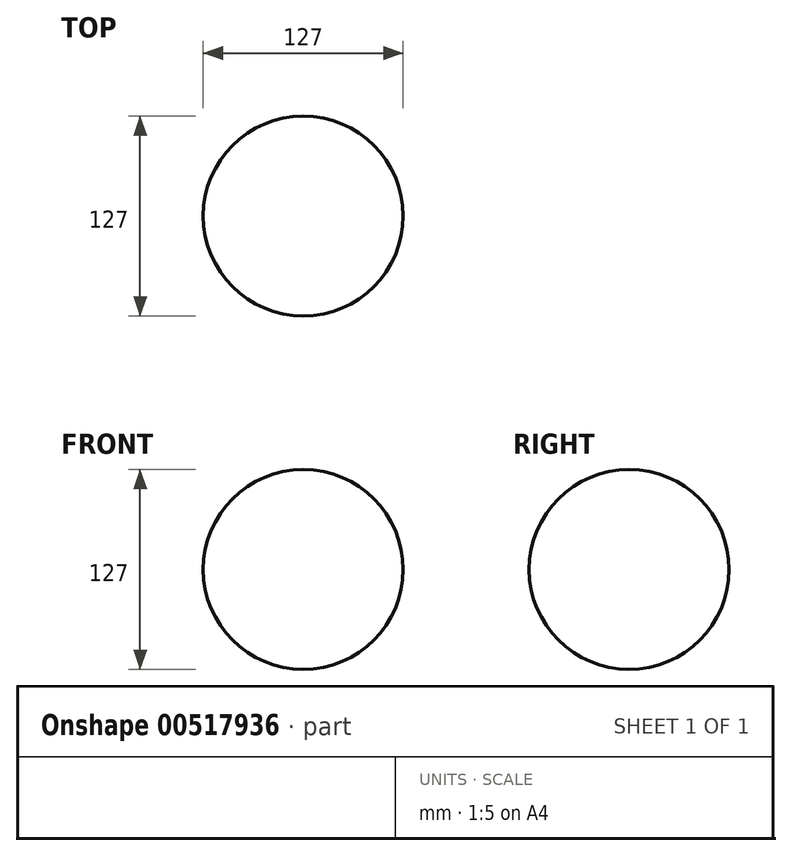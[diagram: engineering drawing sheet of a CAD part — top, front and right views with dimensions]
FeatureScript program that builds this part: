
annotation { "Feature Type Name" : "Feature", "Feature Type Description" : "" }
export const myFeature = defineFeature(function(context is Context, id is Id, definition is map)
    precondition{}
    {
        {
            var Q0;
            Q0=qCreatedBy(makeId("Front.planeOp"),FACE);
            var sketch = newSketch(context, id + "F0", { "sketchPlane" : qUnion([Q0])});
            skArc(sketch, "E0", {"start": v(63.5, 0) * mm, "mid": v(44.9, 44.9) * mm, "end": v(0, 63.5) * mm});
            skArc(sketch, "E1", {"start": v(0, -63.5) * mm, "mid": v(44.9, -44.9) * mm, "end": v(63.5, 0) * mm});
            skLineSegment(sketch, "E2", {"start": v(0, 63.5) * mm, "end": v(0, -63.5) * mm});
            skSolve(sketch);
        }
        {
            var Q0;
            Q0=makeQuery(id+"F0.imprint","IMPRINT",FACE,{"disambiguationData":[TD([[makeQuery(id+"F0.imprint","IMPRINT",EDGE,{"derivedFrom":sQuery(id+"F0.wireOp",EDGE,"E0")}),1.0]])]});
            var Q1;
            Q1=sQuery(id+"F0.wireOp",EDGE,"E2");
            revolve(context, id + "F1", {"entities" : qUnion([Q0]), "axis" : qUnion([Q1]), "revolveType" : RevolveType.FULL});
        }
    });
